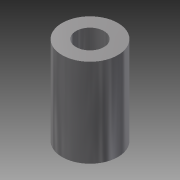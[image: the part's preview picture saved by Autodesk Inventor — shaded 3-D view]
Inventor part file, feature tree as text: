
AUTODESK INVENTOR PART (.ipt)
format: ipt  version: 2015 (Build 190159000, 159)  size: 108,032 bytes
history: native  units: mm
features: extrude x1, sketch x1
ambient origin geometry x8: Origin, YZ Plane, XZ Plane, XY Plane, X Axis, Y Axis, Z Axis, Center Point
bodies: Solid1 (feature_tree)
feature tree (2):
  extrude  "Extrusion1"  Depth=19.0mm
  sketch  "Sketch1"  dims[d0=6.0mm d1=12.0mm d2=19.0mm d3=0.0mm]
